annotation { "Feature Type Name" : "Feature", "Feature Type Description" : "" }
export const myFeature = defineFeature(function(context is Context, id is Id, definition is map)
    precondition{}
    {
        {
            var Q0;
            Q0=qCreatedBy(makeId("Top.planeOp"),FACE);
            var sketch = newSketch(context, id + "F0", { "sketchPlane" : qUnion([Q0])});
            skLineSegment(sketch, "E0.bottom", {"start": v(254, 228.6) * mm, "end": v(-254, 228.6) * mm});
            skLineSegment(sketch, "E0.top", {"start": v(254, -228.6) * mm, "end": v(-254, -228.6) * mm});
            skLineSegment(sketch, "E0.left", {"start": v(254, 228.6) * mm, "end": v(254, -228.6) * mm});
            skLineSegment(sketch, "E0.right", {"start": v(-254, 228.6) * mm, "end": v(-254, -228.6) * mm});
            skPoint(sketch, "E0.middle", {"position": v(0, 0) * mm});
            skPoint(sketch, "E1.endSnap0", {"position": v(-254, 0) * mm});
            skPoint(sketch, "E2.middle", {"position": v(-212.72, 0) * mm});
            skLineSegment(sketch, "E3", {"start": v(-254, 0) * mm, "end": v(-212.72, 0) * mm});
            skLineSegment(sketch, "E4.bottom", {"start": v(-219.07, 50.8) * mm, "end": v(-206.37, 50.8) * mm});
            skLineSegment(sketch, "E4.top", {"start": v(-219.07, -50.8) * mm, "end": v(-206.37, -50.8) * mm});
            skLineSegment(sketch, "E4.left", {"start": v(-228.6, 41.28) * mm, "end": v(-228.6, -41.27) * mm});
            skLineSegment(sketch, "E4.right", {"start": v(-196.85, 41.28) * mm, "end": v(-196.85, -41.27) * mm});
            skPoint(sketch, "E5.visualSharp", {"position": v(-228.6, 50.8) * mm});
            skArc(sketch, "E5.filletArc", {"start": v(-219.07, 50.8) * mm, "mid": v(-225.81, 48.01) * mm, "end": v(-228.6, 41.28) * mm});
            skPoint(sketch, "E6.visualSharp", {"position": v(-196.85, 50.8) * mm});
            skArc(sketch, "E6.filletArc", {"start": v(-196.85, 41.28) * mm, "mid": v(-199.64, 48.01) * mm, "end": v(-206.37, 50.8) * mm});
            skPoint(sketch, "E7.visualSharp", {"position": v(-196.85, -50.8) * mm});
            skArc(sketch, "E7.filletArc", {"start": v(-206.37, -50.8) * mm, "mid": v(-199.64, -48.01) * mm, "end": v(-196.85, -41.27) * mm});
            skPoint(sketch, "E8.visualSharp", {"position": v(-228.6, -50.8) * mm});
            skArc(sketch, "E8.filletArc", {"start": v(-228.6, -41.27) * mm, "mid": v(-225.81, -48.01) * mm, "end": v(-219.07, -50.8) * mm});
            skCircle(sketch, "E9", {"center": v(0, 0) * mm, "radius": 7.14 * mm});
            skLineSegment(sketch, "E10.bottom", {"start": v(190.5, 190.5) * mm, "end": v(-190.5, 190.5) * mm});
            skLineSegment(sketch, "E10.top", {"start": v(190.5, -190.5) * mm, "end": v(-190.5, -190.5) * mm});
            skLineSegment(sketch, "E10.left", {"start": v(190.5, 190.5) * mm, "end": v(190.5, -190.5) * mm});
            skLineSegment(sketch, "E10.right", {"start": v(-190.5, 190.5) * mm, "end": v(-190.5, -190.5) * mm});
            skCircle(sketch, "E11", {"center": v(-190.5, 190.5) * mm, "radius": 7.14 * mm});
            skCircle(sketch, "E12", {"center": v(190.5, 190.5) * mm, "radius": 7.14 * mm});
            skCircle(sketch, "E13", {"center": v(-190.5, -190.5) * mm, "radius": 7.14 * mm});
            skCircle(sketch, "E14", {"center": v(190.5, -190.5) * mm, "radius": 7.14 * mm});
            skLineSegment(sketch, "E15.bottom", {"start": v(136.53, 139.7) * mm, "end": v(-136.53, 139.7) * mm});
            skLineSegment(sketch, "E15.top", {"start": v(136.52, -139.7) * mm, "end": v(-136.53, -139.7) * mm});
            skLineSegment(sketch, "E15.left", {"start": v(139.7, 136.52) * mm, "end": v(139.7, -136.53) * mm});
            skLineSegment(sketch, "E15.right", {"start": v(-139.7, 136.53) * mm, "end": v(-139.7, -136.52) * mm});
            skPoint(sketch, "E16.visualSharp", {"position": v(-139.7, 139.7) * mm});
            skArc(sketch, "E16.filletArc", {"start": v(-136.53, 139.7) * mm, "mid": v(-138.77, 138.77) * mm, "end": v(-139.7, 136.53) * mm});
            skPoint(sketch, "E17.visualSharp", {"position": v(139.7, 139.7) * mm});
            skArc(sketch, "E17.filletArc", {"start": v(139.7, 136.52) * mm, "mid": v(138.77, 138.77) * mm, "end": v(136.53, 139.7) * mm});
            skPoint(sketch, "E18.visualSharp", {"position": v(139.7, -139.7) * mm});
            skArc(sketch, "E18.filletArc", {"start": v(136.52, -139.7) * mm, "mid": v(138.77, -138.77) * mm, "end": v(139.7, -136.53) * mm});
            skPoint(sketch, "E19.visualSharp", {"position": v(-139.7, -139.7) * mm});
            skArc(sketch, "E19.filletArc", {"start": v(-139.7, -136.52) * mm, "mid": v(-138.77, -138.77) * mm, "end": v(-136.53, -139.7) * mm});
            skSolve(sketch);
        }
        {
            var Q0;
            {var subQ20=sQuery(id+"F0.wireOp",EDGE,"E0.bottom");Q0=makeQuery(id+"F0.imprint","IMPRINT",FACE,{"disambiguationData":[TD([[makeQuery(id+"F0.imprint","IMPRINT",EDGE,{"derivedFrom":subQ20}),1.0]])]});}
            var Q1;
            Q1=makeQuery(id+"F0.imprint","IMPRINT",FACE,{"disambiguationData":[TD([[makeQuery(id+"F0.imprint","IMPRINT",EDGE,{"derivedFrom":sQuery(id+"F0.wireOp",EDGE,"E15.bottom")}),-1.0]])]});
            extrude(context, id + "F1", {"entities" : qUnion([Q0, Q1]), "depth" : 1.59 * mm, "offsetDistance" : 25.4 * mm});
        }
        {
            var Q0;
            Q0=qCreatedBy(makeId("Top.planeOp"),FACE);
            var sketch = newSketch(context, id + "F2", { "sketchPlane" : qUnion([Q0])});
            skLineSegment(sketch, "E20.bottom", {"start": v(253.15, -259.7) * mm, "end": v(-254.85, -259.7) * mm});
            skLineSegment(sketch, "E20.top", {"start": v(253.15, -716.9) * mm, "end": v(-254.85, -716.9) * mm});
            skLineSegment(sketch, "E20.left", {"start": v(253.15, -259.7) * mm, "end": v(253.15, -716.9) * mm});
            skLineSegment(sketch, "E20.right", {"start": v(-254.85, -259.7) * mm, "end": v(-254.85, -716.9) * mm});
            skPoint(sketch, "E20.middle", {"position": v(-0.85, -488.3) * mm});
            skPoint(sketch, "E21.endSnap0", {"position": v(-254.85, -488.3) * mm});
            skPoint(sketch, "E22.middle", {"position": v(-213.57, -488.3) * mm});
            skLineSegment(sketch, "E23", {"start": v(-254.85, -488.3) * mm, "end": v(-213.57, -488.3) * mm});
            skLineSegment(sketch, "E24.bottom", {"start": v(-219.92, -437.5) * mm, "end": v(-207.22, -437.5) * mm});
            skLineSegment(sketch, "E24.top", {"start": v(-219.92, -539.1) * mm, "end": v(-207.22, -539.1) * mm});
            skLineSegment(sketch, "E24.left", {"start": v(-229.45, -447.03) * mm, "end": v(-229.45, -529.58) * mm});
            skLineSegment(sketch, "E24.right", {"start": v(-197.7, -447.03) * mm, "end": v(-197.7, -529.58) * mm});
            skPoint(sketch, "E25.visualSharp", {"position": v(-229.45, -437.5) * mm});
            skArc(sketch, "E25.filletArc", {"start": v(-219.92, -437.5) * mm, "mid": v(-226.66, -440.3) * mm, "end": v(-229.45, -447.03) * mm});
            skPoint(sketch, "E26.visualSharp", {"position": v(-197.7, -437.5) * mm});
            skArc(sketch, "E26.filletArc", {"start": v(-197.7, -447.03) * mm, "mid": v(-200.49, -440.3) * mm, "end": v(-207.22, -437.5) * mm});
            skPoint(sketch, "E27.visualSharp", {"position": v(-197.7, -539.1) * mm});
            skArc(sketch, "E27.filletArc", {"start": v(-207.22, -539.1) * mm, "mid": v(-200.49, -536.31) * mm, "end": v(-197.7, -529.58) * mm});
            skPoint(sketch, "E28.visualSharp", {"position": v(-229.45, -539.1) * mm});
            skArc(sketch, "E28.filletArc", {"start": v(-229.45, -529.58) * mm, "mid": v(-226.66, -536.31) * mm, "end": v(-219.92, -539.1) * mm});
            skLineSegment(sketch, "E29.bottom", {"start": v(189.65, -297.8) * mm, "end": v(-191.35, -297.8) * mm});
            skLineSegment(sketch, "E29.top", {"start": v(189.65, -678.8) * mm, "end": v(-191.35, -678.8) * mm});
            skLineSegment(sketch, "E29.left", {"start": v(189.65, -297.8) * mm, "end": v(189.65, -678.8) * mm});
            skLineSegment(sketch, "E29.right", {"start": v(-191.35, -297.8) * mm, "end": v(-191.35, -678.8) * mm});
            skCircle(sketch, "E30", {"center": v(-191.35, -297.8) * mm, "radius": 7.14 * mm});
            skCircle(sketch, "E31", {"center": v(189.65, -297.8) * mm, "radius": 7.14 * mm});
            skCircle(sketch, "E32", {"center": v(-191.35, -678.8) * mm, "radius": 7.14 * mm});
            skCircle(sketch, "E33", {"center": v(189.65, -678.8) * mm, "radius": 7.14 * mm});
            skLineSegment(sketch, "E34.bottom", {"start": v(122.98, -361.3) * mm, "end": v(2.33, -361.3) * mm});
            skLineSegment(sketch, "E34.top", {"start": v(-4.02, -615.3) * mm, "end": v(-124.67, -615.3) * mm});
            skLineSegment(sketch, "E34.left", {"start": v(126.15, -364.48) * mm, "end": v(126.15, -485.13) * mm});
            skLineSegment(sketch, "E34.right", {"start": v(-127.85, -491.48) * mm, "end": v(-127.85, -612.13) * mm});
            skLineSegment(sketch, "E35.top", {"start": v(-124.67, -488.3) * mm, "end": v(-10.67, -488.3) * mm});
            skLineSegment(sketch, "E35.right", {"start": v(-0.85, -364.48) * mm, "end": v(-0.85, -478.48) * mm});
            skLineSegment(sketch, "E36.bottom", {"start": v(8.97, -488.3) * mm, "end": v(122.98, -488.3) * mm});
            skLineSegment(sketch, "E36.left", {"start": v(-0.85, -498.12) * mm, "end": v(-0.85, -612.13) * mm});
            skPoint(sketch, "E35.left.start.orphan", {"position": v(-127.85, -361.3) * mm});
            skPoint(sketch, "E37.orphan", {"position": v(126.15, -615.3) * mm});
            skPoint(sketch, "E38.visualSharp", {"position": v(126.15, -361.3) * mm});
            skArc(sketch, "E38.filletArc", {"start": v(126.15, -364.48) * mm, "mid": v(125.22, -362.23) * mm, "end": v(122.98, -361.3) * mm});
            skPoint(sketch, "E39.visualSharp", {"position": v(-0.85, -361.3) * mm});
            skPoint(sketch, "E40.visualSharp", {"position": v(126.15, -488.3) * mm});
            skPoint(sketch, "E41.visualSharp", {"position": v(-127.85, -488.3) * mm});
            skPoint(sketch, "E42.visualSharp", {"position": v(-127.85, -615.3) * mm});
            skArc(sketch, "E42.filletArc", {"start": v(-127.85, -612.13) * mm, "mid": v(-126.92, -614.37) * mm, "end": v(-124.67, -615.3) * mm});
            skPoint(sketch, "E43.visualSharp", {"position": v(-8, -488.3) * mm});
            skPoint(sketch, "E44.visualSharp", {"position": v(-0.85, -495.45) * mm});
            skArc(sketch, "E45", {"start": v(-0.85, -495.45) * mm, "mid": v(4.2, -493.35) * mm, "end": v(6.3, -488.3) * mm});
            skLineSegment(sketch, "E46", {"start": v(-0.85, -478.48) * mm, "end": v(-0.85, -481.16) * mm});
            skLineSegment(sketch, "E47", {"start": v(8.97, -488.3) * mm, "end": v(6.3, -488.3) * mm});
            skLineSegment(sketch, "E48", {"start": v(-0.85, -498.12) * mm, "end": v(-0.85, -495.45) * mm});
            skLineSegment(sketch, "E49", {"start": v(-8, -488.3) * mm, "end": v(-10.67, -488.3) * mm});
            skArc(sketch, "E50.trimOffspring", {"start": v(-0.85, -481.16) * mm, "mid": v(-5.9, -483.25) * mm, "end": v(-8, -488.3) * mm});
            skLineSegment(sketch, "E51", {"start": v(-127.85, -491.48) * mm, "end": v(-127.85, -488.3) * mm});
            skLineSegment(sketch, "E52", {"start": v(-124.67, -488.3) * mm, "end": v(-127.85, -488.3) * mm});
            skLineSegment(sketch, "E53", {"start": v(-0.85, -612.13) * mm, "end": v(-0.85, -615.3) * mm});
            skLineSegment(sketch, "E54", {"start": v(-0.85, -615.3) * mm, "end": v(-4.02, -615.3) * mm});
            skLineSegment(sketch, "E55", {"start": v(-0.85, -361.3) * mm, "end": v(-0.85, -364.48) * mm});
            skLineSegment(sketch, "E56", {"start": v(2.33, -361.3) * mm, "end": v(-0.85, -361.3) * mm});
            skLineSegment(sketch, "E57", {"start": v(122.98, -488.3) * mm, "end": v(126.15, -488.3) * mm});
            skLineSegment(sketch, "E58", {"start": v(126.15, -485.13) * mm, "end": v(126.15, -488.3) * mm});
            skSolve(sketch);
        }
        {
            var Q0;
            {var subQ14=sQuery(id+"F2.wireOp",EDGE,"E20.bottom");Q0=makeQuery(id+"F2.imprint","IMPRINT",FACE,{"disambiguationData":[TD([[makeQuery(id+"F2.imprint","IMPRINT",EDGE,{"derivedFrom":subQ14}),1.0]])]});}
            var Q1;
            Q1=makeQuery(id+"F2.imprint","IMPRINT",FACE,{"disambiguationData":[TD([[makeQuery(id+"F2.imprint","IMPRINT",EDGE,{"derivedFrom":sQuery(id+"F2.wireOp",EDGE,"E34.bottom")}),-1.0]])]});
            var Q2;
            {var subQ4=sQuery(id+"F2.wireOp",EDGE,"E35.bottom");Q2=makeQuery(id+"F2.imprint","IMPRINT",FACE,{"disambiguationData":[TD([[makeQuery(id+"F2.imprint","IMPRINT",EDGE,{"derivedFrom":subQ4}),-1.0]])]});}
            var Q3;
            {var subQ0=sQuery(id+"F2.wireOp",EDGE,"E36.top");Q3=makeQuery(id+"F2.imprint","IMPRINT",FACE,{"disambiguationData":[TD([[makeQuery(id+"F2.imprint","IMPRINT",EDGE,{"derivedFrom":subQ0}),1.0]])]});}
            extrude(context, id + "F3", {"entities" : qUnion([Q0, Q1, Q2, Q3]), "depth" : 1.59 * mm, "offsetDistance" : 25.4 * mm});
        }
        {
            var Q0;
            Q0=qCreatedBy(makeId("Top.planeOp"),FACE);
            var sketch = newSketch(context, id + "F4", { "sketchPlane" : qUnion([Q0])});
            skLineSegment(sketch, "E59.bottom", {"start": v(251.94, -750.64) * mm, "end": v(-256.06, -750.64) * mm});
            skLineSegment(sketch, "E59.top", {"start": v(251.94, -1207.84) * mm, "end": v(-256.06, -1207.84) * mm});
            skLineSegment(sketch, "E59.left", {"start": v(251.94, -750.64) * mm, "end": v(251.94, -1207.84) * mm});
            skLineSegment(sketch, "E59.right", {"start": v(-256.06, -750.64) * mm, "end": v(-256.06, -1207.84) * mm});
            skPoint(sketch, "E59.middle", {"position": v(-2.06, -979.24) * mm});
            skPoint(sketch, "E60.endSnap0", {"position": v(-256.06, -979.24) * mm});
            skPoint(sketch, "E61.middle", {"position": v(-214.79, -979.24) * mm});
            skLineSegment(sketch, "E62", {"start": v(-256.06, -979.24) * mm, "end": v(-214.79, -979.24) * mm});
            skLineSegment(sketch, "E63.bottom", {"start": v(-221.14, -928.44) * mm, "end": v(-208.44, -928.44) * mm});
            skLineSegment(sketch, "E63.top", {"start": v(-221.14, -1030.04) * mm, "end": v(-208.44, -1030.04) * mm});
            skLineSegment(sketch, "E63.left", {"start": v(-230.66, -937.97) * mm, "end": v(-230.66, -1020.52) * mm});
            skLineSegment(sketch, "E63.right", {"start": v(-198.91, -937.97) * mm, "end": v(-198.91, -1020.52) * mm});
            skPoint(sketch, "E64.visualSharp", {"position": v(-230.66, -928.44) * mm});
            skArc(sketch, "E64.filletArc", {"start": v(-221.14, -928.44) * mm, "mid": v(-227.87, -931.23) * mm, "end": v(-230.66, -937.97) * mm});
            skPoint(sketch, "E65.visualSharp", {"position": v(-198.91, -928.44) * mm});
            skArc(sketch, "E65.filletArc", {"start": v(-198.91, -937.97) * mm, "mid": v(-201.7, -931.23) * mm, "end": v(-208.44, -928.44) * mm});
            skPoint(sketch, "E66.visualSharp", {"position": v(-198.91, -1030.04) * mm});
            skArc(sketch, "E66.filletArc", {"start": v(-208.44, -1030.04) * mm, "mid": v(-201.7, -1027.25) * mm, "end": v(-198.91, -1020.52) * mm});
            skPoint(sketch, "E67.visualSharp", {"position": v(-230.66, -1030.04) * mm});
            skArc(sketch, "E67.filletArc", {"start": v(-230.66, -1020.52) * mm, "mid": v(-227.87, -1027.25) * mm, "end": v(-221.14, -1030.04) * mm});
            skCircle(sketch, "E68", {"center": v(-2.06, -979.24) * mm, "radius": 7.14 * mm});
            skLineSegment(sketch, "E69.bottom", {"start": v(188.44, -788.74) * mm, "end": v(-192.56, -788.74) * mm});
            skLineSegment(sketch, "E69.top", {"start": v(188.44, -1169.74) * mm, "end": v(-192.56, -1169.74) * mm});
            skLineSegment(sketch, "E69.left", {"start": v(188.44, -788.74) * mm, "end": v(188.44, -1169.74) * mm});
            skLineSegment(sketch, "E69.right", {"start": v(-192.56, -788.74) * mm, "end": v(-192.56, -1169.74) * mm});
            skCircle(sketch, "E70", {"center": v(-192.56, -788.74) * mm, "radius": 7.14 * mm});
            skCircle(sketch, "E71", {"center": v(188.44, -788.74) * mm, "radius": 7.14 * mm});
            skCircle(sketch, "E72", {"center": v(-192.56, -1169.74) * mm, "radius": 7.14 * mm});
            skCircle(sketch, "E73", {"center": v(188.44, -1169.74) * mm, "radius": 7.14 * mm});
            skLineSegment(sketch, "E74.bottom", {"start": v(124.94, -852.24) * mm, "end": v(-129.06, -852.24) * mm});
            skLineSegment(sketch, "E74.top", {"start": v(124.94, -1106.24) * mm, "end": v(-129.06, -1106.24) * mm});
            skLineSegment(sketch, "E74.left", {"start": v(124.94, -852.24) * mm, "end": v(124.94, -1106.24) * mm});
            skLineSegment(sketch, "E74.right", {"start": v(-129.06, -852.24) * mm, "end": v(-129.06, -1106.24) * mm});
            skCircle(sketch, "E75", {"center": v(-2.06, -979.24) * mm, "radius": 25.4 * mm});
            skSolve(sketch);
        }
        {
            var Q0;
            {var subQ20=sQuery(id+"F4.wireOp",EDGE,"E59.bottom");Q0=makeQuery(id+"F4.imprint","IMPRINT",FACE,{"disambiguationData":[TD([[makeQuery(id+"F4.imprint","IMPRINT",EDGE,{"derivedFrom":subQ20}),1.0]])]});}
            var Q1;
            Q1=makeQuery(id+"F4.imprint","IMPRINT",FACE,{"disambiguationData":[TD([[makeQuery(id+"F4.imprint","IMPRINT",EDGE,{"derivedFrom":sQuery(id+"F4.wireOp",EDGE,"E74.bottom")}),-1.0]])]});
            var Q2;
            Q2=makeQuery(id+"F4.imprint","IMPRINT",FACE,{"disambiguationData":[TD([[makeQuery(id+"F4.imprint","IMPRINT",EDGE,{"derivedFrom":sQuery(id+"F4.wireOp",EDGE,"E74.bottom")}),1.0]])]});
            extrude(context, id + "F5", {"entities" : qUnion([Q0, Q1, Q2]), "depth" : 1.59 * mm, "offsetDistance" : 25.4 * mm});
        }
        {
            var Q0;
            Q0=qCreatedBy(makeId("Top.planeOp"),FACE);
            var sketch = newSketch(context, id + "F6", { "sketchPlane" : qUnion([Q0])});
            skPoint(sketch, "E76.endSnap0", {"position": v(-254, -1375.1) * mm});
            skPoint(sketch, "E77.middle", {"position": v(0, -1289.53) * mm});
            skLineSegment(sketch, "E78.bottom", {"start": v(50.8, -1283.18) * mm, "end": v(50.8, -1295.88) * mm});
            skLineSegment(sketch, "E78.top", {"start": v(-50.8, -1283.18) * mm, "end": v(-50.8, -1295.88) * mm});
            skLineSegment(sketch, "E78.left", {"start": v(41.28, -1273.65) * mm, "end": v(-41.28, -1273.65) * mm});
            skLineSegment(sketch, "E78.right", {"start": v(41.27, -1305.4) * mm, "end": v(-41.28, -1305.4) * mm});
            skPoint(sketch, "E79.visualSharp", {"position": v(50.8, -1273.65) * mm});
            skArc(sketch, "E79.filletArc", {"start": v(50.8, -1283.18) * mm, "mid": v(48.01, -1276.44) * mm, "end": v(41.27, -1273.65) * mm});
            skPoint(sketch, "E80.visualSharp", {"position": v(50.8, -1305.4) * mm});
            skArc(sketch, "E80.filletArc", {"start": v(41.27, -1305.4) * mm, "mid": v(48.01, -1302.61) * mm, "end": v(50.8, -1295.88) * mm});
            skPoint(sketch, "E81.visualSharp", {"position": v(-50.8, -1305.4) * mm});
            skArc(sketch, "E81.filletArc", {"start": v(-50.8, -1295.88) * mm, "mid": v(-48.01, -1302.61) * mm, "end": v(-41.28, -1305.4) * mm});
            skPoint(sketch, "E82.visualSharp", {"position": v(-50.8, -1273.65) * mm});
            skArc(sketch, "E82.filletArc", {"start": v(-41.28, -1273.65) * mm, "mid": v(-48.01, -1276.44) * mm, "end": v(-50.8, -1283.18) * mm});
            skPoint(sketch, "E83.middle", {"position": v(0, -1375.1) * mm});
            skLineSegment(sketch, "E84.bottom", {"start": v(126.52, -1248.25) * mm, "end": v(-126.52, -1248.25) * mm});
            skLineSegment(sketch, "E84.top", {"start": v(126.52, -1501.93) * mm, "end": v(-126.52, -1501.93) * mm});
            skLineSegment(sketch, "E85.bottom", {"start": v(254, -1248.1) * mm, "end": v(-254, -1248.1) * mm});
            skLineSegment(sketch, "E85.top", {"start": v(254, -1502.1) * mm, "end": v(-254, -1502.1) * mm});
            skLineSegment(sketch, "E85.left", {"start": v(254, -1248.1) * mm, "end": v(254, -1502.1) * mm});
            skLineSegment(sketch, "E85.right", {"start": v(-254, -1248.1) * mm, "end": v(-254, -1502.1) * mm});
            skLineSegment(sketch, "E86", {"start": v(0, -1248.25) * mm, "end": v(0, -1289.53) * mm});
            skText(sketch, "E87", { "text": "SURVEY MONUMENT", "fontName": "AllertaStencil-Regular.ttf"});
            skText(sketch, "E88", { "text": "DO NOT MOVE", "fontName": "AllertaStencil-Regular.ttf"});
            skLineSegment(sketch, "E89.bottom", {"start": v(190.5, -1470.34) * mm, "end": v(-190.5, -1470.34) * mm});
            skLineSegment(sketch, "E89.top", {"start": v(190.5, -1279.84) * mm, "end": v(-190.5, -1279.84) * mm});
            skLineSegment(sketch, "E89.left", {"start": v(190.5, -1470.34) * mm, "end": v(190.5, -1279.84) * mm});
            skLineSegment(sketch, "E89.right", {"start": v(-190.5, -1470.34) * mm, "end": v(-190.5, -1279.84) * mm});
            skPoint(sketch, "E89.middle.positionSnap0", {"position": v(0, -1501.93) * mm});
            skPoint(sketch, "E89.centerSnap0", {"position": v(0, -1501.93) * mm});
            skCircle(sketch, "E90", {"center": v(-190.5, -1279.84) * mm, "radius": 7.14 * mm});
            skCircle(sketch, "E91", {"center": v(190.5, -1279.84) * mm, "radius": 7.14 * mm});
            skCircle(sketch, "E92", {"center": v(190.5, -1470.34) * mm, "radius": 7.14 * mm});
            skCircle(sketch, "E93", {"center": v(-190.5, -1470.34) * mm, "radius": 7.14 * mm});
            const initialGuessF6  = {"E87": [-0.19764, -1.3995, 1, 0, 0.02853], "E88": [-0.14125, -1.45108, 1, 0, 0.0288]};
            skSetInitialGuess(sketch, initialGuessF6);
            skSolve(sketch);
        }
        {
            var Q0;
            Q0=makeQuery(id+"F6.imprint","IMPRINT",FACE,{"disambiguationData":[TD([[makeQuery(id+"F6.imprint","IMPRINT",EDGE,{"derivedFrom":sQuery(id+"F6.wireOp",EDGE,"E85.bottom")}),1.0]])]});
            var Q1;
            {var subQ10=sQuery(id+"F6.wireOp",EDGE,"E78.bottom");Q1=makeQuery(id+"F6.imprint","IMPRINT",FACE,{"disambiguationData":[TD([[makeQuery(id+"F6.imprint","IMPRINT",EDGE,{"derivedFrom":subQ10}),1.0]])]});}
            extrude(context, id + "F7", {"entities" : qUnion([Q0, Q1]), "depth" : 1.59 * mm, "offsetDistance" : 25.4 * mm});
        }
        {
            var Q0;
            Q0=qCreatedBy(makeId("Top.planeOp"),FACE);
            var sketch = newSketch(context, id + "F8", { "sketchPlane" : qUnion([Q0])});
            skLineSegment(sketch, "E94.bottom", {"start": v(-173.89, -1846.14) * mm, "end": v(92.81, -1846.14) * mm});
            skLineSegment(sketch, "E94.top", {"start": v(-173.89, -1566.74) * mm, "end": v(92.81, -1566.74) * mm});
            skLineSegment(sketch, "E94.left", {"start": v(-180.24, -1839.8) * mm, "end": v(-180.24, -1573.1) * mm});
            skLineSegment(sketch, "E94.right", {"start": v(99.16, -1839.8) * mm, "end": v(99.16, -1573.1) * mm});
            skPoint(sketch, "E95.visualSharp", {"position": v(-180.24, -1566.74) * mm});
            skArc(sketch, "E95.filletArc", {"start": v(-173.89, -1566.74) * mm, "mid": v(-178.38, -1568.6) * mm, "end": v(-180.24, -1573.1) * mm});
            skPoint(sketch, "E96.visualSharp", {"position": v(99.16, -1566.74) * mm});
            skArc(sketch, "E96.filletArc", {"start": v(99.16, -1573.1) * mm, "mid": v(97.3, -1568.6) * mm, "end": v(92.81, -1566.74) * mm});
            skPoint(sketch, "E97.visualSharp", {"position": v(-180.24, -1846.14) * mm});
            skArc(sketch, "E97.filletArc", {"start": v(-180.24, -1839.8) * mm, "mid": v(-178.38, -1844.28) * mm, "end": v(-173.89, -1846.14) * mm});
            skPoint(sketch, "E98.visualSharp", {"position": v(99.16, -1846.14) * mm});
            skArc(sketch, "E98.filletArc", {"start": v(92.81, -1846.14) * mm, "mid": v(97.3, -1844.28) * mm, "end": v(99.16, -1839.8) * mm});
            skCircle(sketch, "E99", {"center": v(-40.54, -1706.44) * mm, "radius": 7.14 * mm});
            skPoint(sketch, "E99.centerSnap0", {"position": v(-40.54, -1566.74) * mm});
            skPoint(sketch, "E99.centerSnap1", {"position": v(-180.24, -1706.44) * mm});
            skSolve(sketch);
        }
        {
            var Q0;
            Q0=makeQuery(id+"F8.imprint","IMPRINT",FACE,{"disambiguationData":[TD([[makeQuery(id+"F8.imprint","IMPRINT",EDGE,{"derivedFrom":sQuery(id+"F8.wireOp",EDGE,"E94.bottom")}),1.0]])]});
            extrude(context, id + "F9", {"entities" : qUnion([Q0]), "depth" : 1.59 * mm, "offsetDistance" : 25.4 * mm});
        }
    });